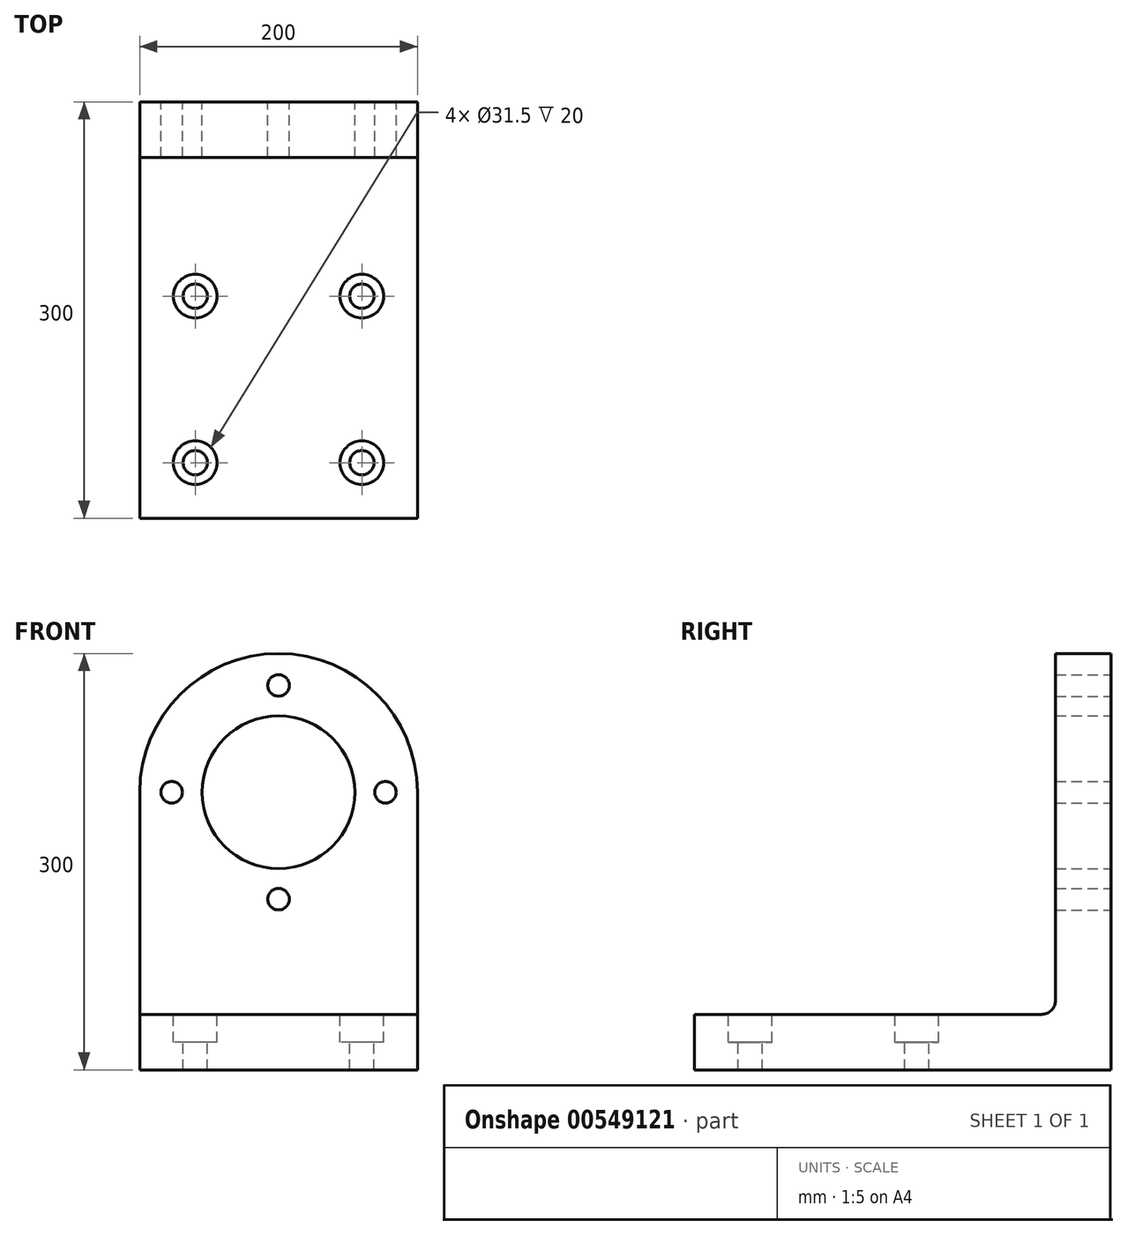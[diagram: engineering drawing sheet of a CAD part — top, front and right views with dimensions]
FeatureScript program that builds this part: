
annotation { "Feature Type Name" : "Feature", "Feature Type Description" : "" }
export const myFeature = defineFeature(function(context is Context, id is Id, definition is map)
    precondition{}
    {
        {
            var Q0;
            Q0=qCreatedBy(makeId("Front.planeOp"),FACE);
            var sketch = newSketch(context, id + "F0", { "sketchPlane" : qUnion([Q0])});
            skLineSegment(sketch, "E0", {"start": v(0, 0) * mm, "end": v(100, 0) * mm});
            skLineSegment(sketch, "E1", {"start": v(0, 0) * mm, "end": v(-98.92, 0) * mm});
            skLineSegment(sketch, "E2.bottom", {"start": v(-98.92, 0) * mm, "end": v(-100, 0) * mm});
            skLineSegment(sketch, "E2.top", {"start": v(100, 200) * mm, "end": v(-100, 200) * mm, "construction": true});
            skLineSegment(sketch, "E2.left", {"start": v(100, 0) * mm, "end": v(100, 200) * mm});
            skLineSegment(sketch, "E2.right", {"start": v(-100, 0) * mm, "end": v(-100, 200) * mm});
            skArc(sketch, "E3", {"start": v(100, 200) * mm, "mid": v(0, 300) * mm, "end": v(-100, 200) * mm});
            skCircle(sketch, "E4", {"center": v(0, 200) * mm, "radius": 55 * mm});
            skLineSegment(sketch, "E5", {"start": v(-100, 40) * mm, "end": v(100, 40) * mm});
            skPoint(sketch, "E6", {"position": v(0, 277) * mm});
            skPoint(sketch, "E7", {"position": v(0, 123) * mm});
            skPoint(sketch, "E8", {"position": v(-77, 200) * mm});
            skPoint(sketch, "E9", {"position": v(77, 200) * mm});
            skSolve(sketch);
        }
        {
            var Q0;
            {var subQ0=sQuery(id+"F0.wireOp",EDGE,"E3");Q0=makeQuery(id+"F0.imprint","IMPRINT",FACE,{"disambiguationData":[TD([[makeQuery(id+"F0.imprint","IMPRINT",EDGE,{"derivedFrom":subQ0}),1.0]])]});}
            extrude(context, id + "F1", {"entities" : qUnion([Q0]), "depth" : 40 * mm, "offsetDistance" : 25 * mm});
        }
        {
            var Q0;
            {var subQ1=sQuery(id+"F0.wireOp",EDGE,"E0");Q0=makeQuery(id+"F0.imprint","IMPRINT",FACE,{"disambiguationData":[TD([[makeQuery(id+"F0.imprint","IMPRINT",EDGE,{"derivedFrom":subQ1}),1.0]])]});}
            extrude(context, id + "F2", {"entities" : qUnion([Q0]), "operationType" : NewBodyOperationType.ADD, "depth" : 300 * mm, "offsetDistance" : 25 * mm});
        }
        {
            var Q0;
            Q0=sQuery(id+"F0.wireOp",VERTEX,"E6");
            var Q1;
            Q1=sQuery(id+"F0.wireOp",VERTEX,"E8");
            var Q2;
            Q2=sQuery(id+"F0.wireOp",VERTEX,"E9");
            var Q3;
            Q3=sQuery(id+"F0.wireOp",VERTEX,"E7");
            var Q4;
            Q4=makeQuery(id+"F1.opExtrude","SWEPT_BODY",BODY,{"disambiguationData":[OSD([sQuery(id+"F0.wireOp",EDGE,"E2.left"),sQuery(id+"F0.wireOp",EDGE,"E2.right"),sQuery(id+"F0.wireOp",EDGE,"E3"),sQuery(id+"F0.wireOp",EDGE,"E4"),sQuery(id+"F0.wireOp",EDGE,"E5")])]});
            hole(context, id + "F3", {"style" : HoleStyle.SIMPLE, "endStyle" : HoleEndStyle.THROUGH, "oppositeDirection" : true, "standardTappedOrClearance" : lookupTablePath({ "standard" : "ISO", "fit" : "Normal", "size" : "M14", "type" : "Clearance" }), "standardBlindInLast" : lookupTablePath({ "fit" : "Standard", "standard" : "ISO", "size" : "M14", "type" : "Clearance" }), "holeDiameter" : 15.5 * mm, "isTappedThrough" : true, "tappedDepth" : 12 * mm, "tapClearance" : 3, "locations" : qUnion([Q0, Q1, Q2, Q3]), "scope" : qUnion([Q4])});
        }
        {
            var Q0;
            Q0=makeQuery(id+"F2.opExtrude","SWEPT_FACE",FACE,{"disambiguationData":[OSD([sQuery(id+"F0.wireOp",EDGE,"E5")])]});
            var sketch = newSketch(context, id + "F4", { "sketchPlane" : qUnion([Q0])});
            skLineSegment(sketch, "E10.bottom", {"start": v(-60, -140) * mm, "end": v(60, -140) * mm, "construction": true});
            skLineSegment(sketch, "E10.top", {"start": v(-60, -260) * mm, "end": v(60, -260) * mm, "construction": true});
            skLineSegment(sketch, "E10.left", {"start": v(-60, -140) * mm, "end": v(-60, -260) * mm, "construction": true});
            skLineSegment(sketch, "E10.right", {"start": v(60, -140) * mm, "end": v(60, -260) * mm, "construction": true});
            skPoint(sketch, "E11", {"position": v(-60, -140) * mm});
            skPoint(sketch, "E12", {"position": v(60, -140) * mm});
            skPoint(sketch, "E13", {"position": v(-60, -260) * mm});
            skPoint(sketch, "E14", {"position": v(60, -260) * mm});
            skLineSegment(sketch, "E15", {"start": v(-100, -290) * mm, "end": v(-90, -300) * mm});
            skLineSegment(sketch, "E16", {"start": v(90, -300) * mm, "end": v(100, -290) * mm});
            skSolve(sketch);
        }
        {
            var Q0;
            Q0=sQuery(id+"F4.wireOp",VERTEX,"E11");
            var Q1;
            Q1=sQuery(id+"F4.wireOp",VERTEX,"E12");
            var Q2;
            Q2=sQuery(id+"F4.wireOp",VERTEX,"E14");
            var Q3;
            Q3=sQuery(id+"F4.wireOp",VERTEX,"E13");
            var Q4;
            Q4=makeQuery(id+"F1.opExtrude","SWEPT_BODY",BODY,{"disambiguationData":[OSD([sQuery(id+"F0.wireOp",EDGE,"E2.left"),sQuery(id+"F0.wireOp",EDGE,"E2.right"),sQuery(id+"F0.wireOp",EDGE,"E3"),sQuery(id+"F0.wireOp",EDGE,"E4"),sQuery(id+"F0.wireOp",EDGE,"E5")])]});
            hole(context, id + "F5", {"style" : HoleStyle.C_BORE, "endStyle" : HoleEndStyle.THROUGH, "holeDiameter" : 17.5 * mm, "cBoreDiameter" : 31.5 * mm, "cBoreDepth" : 20 * mm, "isTappedThrough" : true, "tappedDepth" : 12 * mm, "tapClearance" : 3, "locations" : qUnion([Q0, Q1, Q2, Q3]), "scope" : qUnion([Q4])});
        }
        {
            var Q0;
            {var subQ0=sQuery(id+"F0.wireOp",EDGE,"E2.left");Q0=makeQuery(id+"F2.boolean.opBoolean","MERGE",FACE,{"derivedFrom":[makeQuery(id+"F1.opExtrude","SWEPT_FACE",FACE,{"disambiguationData":[OSD([subQ0])]}),makeQuery(id+"F2.opExtrude","SWEPT_FACE",FACE,{"disambiguationData":[OSD([subQ0])]})]});}
            var sketch = newSketch(context, id + "F6", { "sketchPlane" : qUnion([Q0])});
            skLineSegment(sketch, "E17", {"start": v(-300, 40) * mm, "end": v(-50, 40) * mm});
            skLineSegment(sketch, "E18", {"start": v(-40, 50) * mm, "end": v(-40, 200) * mm});
            skPoint(sketch, "E19.visualSharp", {"position": v(-40, 40) * mm});
            skArc(sketch, "E19.filletArc", {"start": v(-50, 40) * mm, "mid": v(-42.93, 42.93) * mm, "end": v(-40, 50) * mm});
            skSolve(sketch);
        }
        {
            var Q0;
            {var subQ0=sQuery(id+"F6.wireOp",EDGE,"E19.filletArc");Q0=makeQuery(id+"F6.imprint","IMPRINT",FACE,{"disambiguationData":[TD([[makeQuery(id+"F6.imprint","IMPRINT",EDGE,{"derivedFrom":subQ0}),-1.0]])]});}
            extrude(context, id + "F7", {"entities" : qUnion([Q0]), "operationType" : NewBodyOperationType.ADD, "oppositeDirection" : true, "depth" : 200 * mm, "offsetDistance" : 25 * mm});
        }
    });
